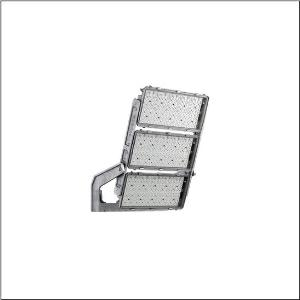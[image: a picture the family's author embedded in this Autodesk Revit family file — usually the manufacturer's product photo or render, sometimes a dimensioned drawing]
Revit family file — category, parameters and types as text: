
# Revit family: floodlight_fl_11_maxi_pro_remote___pl33t_5xa779427f01ba_72f0
name_source: partatom
category: Lighting Fixtures
units: mm (PartAtom-declared; Revit-internal decimal feet)

## family parameters
Cut with Voids When Loaded = No
Host = Face
Light Source = No
Part Type = Normal
Room Calculation Point = No
Round Connector Dimension = Use Diameter
Shared = No

## types (1)
- --- (1 x LED, 132850 lm, 953.7 W, 5000K)
    Apparent Load = 954 VA
    CIE Flux Codes = 25 74 99 100 100
    Color Rendering = 70
    Color Temperature = 5000K
    Default Elevation = 1800 mm
    Description = Floodlight FL 11  maxi  pro Remote floodlight; light control with lens of PMMA; cover panel of toughened safety glass, transparent; light distribution: PL33T, asymmetric direct distribution, LEDcolour temperature: 5000K, rated luminous flux: 132.850lm, colour rendering: CRI > 70, light colour: 750; luminous efficacy: 139lm/W; brightness control: DALI 2 (1 DALI address); with terminal, 8-pole, max. 2.5mm², mains connection: 220..240V/380..400V AC, 50/60Hz, surge voltage resistance: line to ground: 10kV, ECG replaceable separately, no afterglow with DALI off / DMX off command, LED unit replaceable without ESD environment, dustproof LED module, dimming range 10..100%; 954W floodlight with 2x LED unit of diecast aluminium, coated grey; length: 713mm / width: 651mm / height: 338mm; mounting bracket, of diecast aluminium, uncoated, natural, equipment: Longlife, protection rating (complete): IP66; insulation class (complete): insulation class I (protective earthing); certification: CE, ENEC, VDE; ball protection: ball impact resistance with accessories, impact resistance: IK07; only for outdoor installations, rated ambient temperature 10°C, permissible operating ambient temperature: -40..+30°C, permissible storage temperature: -40..+85°C; packaging unit: 1 piece

Light Distribution: PL33T
    Height = 320 mm
    Lamp = 1 x LED
    Lamp Light Flux = 132850 lm
    Lamp Power = 953.7 W
    Lamp count = 1
    Length = 1002 mm
    Luminous efficacy = 139 lm/W
    Manufacturer = Siteco
    ModVariant = No
    Model = 5XA779427F01BA
    Mounting Place = Ceiling
    Mounting Type = Surface mounted
    Number of Poles = 1
    OnlyDefault = Yes
    Power Factor = 1
    Product Name = Floodlight FL 11 maxi pro Remote | PL33T
    Product group = floodlight | ceiling mounted
    ProductGroupID = 302
    Protection Class = Protection class I
    Protection Degree = IP 66
    RLX_Detail_Level = 1
    RLX_Emergency_Light_Flux = 0 lm
    RLX_Emergency_Type = 0
    RLX_Emergency_Type_DB = No
    RlxData = <blob elided: 52385 chars, md5=30216a02>
    Socket = socket
    Standby Power = 0 W
    System Light Flux = 132850 lm
    System Power = 954 W
    Type Comments = factory setting: luminous flux: 100 % | dim-lin: 254 | 665 mA
    Type Image = l_1006784.jpg
    URL = http://relux.com
    VarID = @adj_027435
    Voltage = 0 V
    Weight = 0.00 kg
    Width = 655 mm

## geometry (parser evidence)
native form markers: Blend x4, Sweep x15
no freeform markers — native parametric forms only
